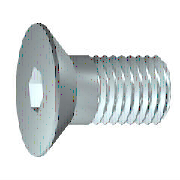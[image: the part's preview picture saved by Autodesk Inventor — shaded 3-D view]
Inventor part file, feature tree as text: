
AUTODESK INVENTOR PART (.ipt)
format: ipt  version: 2024.3 (Build 283343000, 343)  size: 182,784 bytes
history: native  units: mm (DEFAULTED — no unit token found)
features: extrude x1, plane x1
ambient origin geometry x7: Origin, YZ Plane, XY Plane, X Axis, Y Axis, Z Axis, Center Point
bodies: Solid1 (feature_tree), Body (feature_tree)
feature tree (2):
  extrude  "Slot"  Depth=10.0mm
  plane  "Work Plane1"
